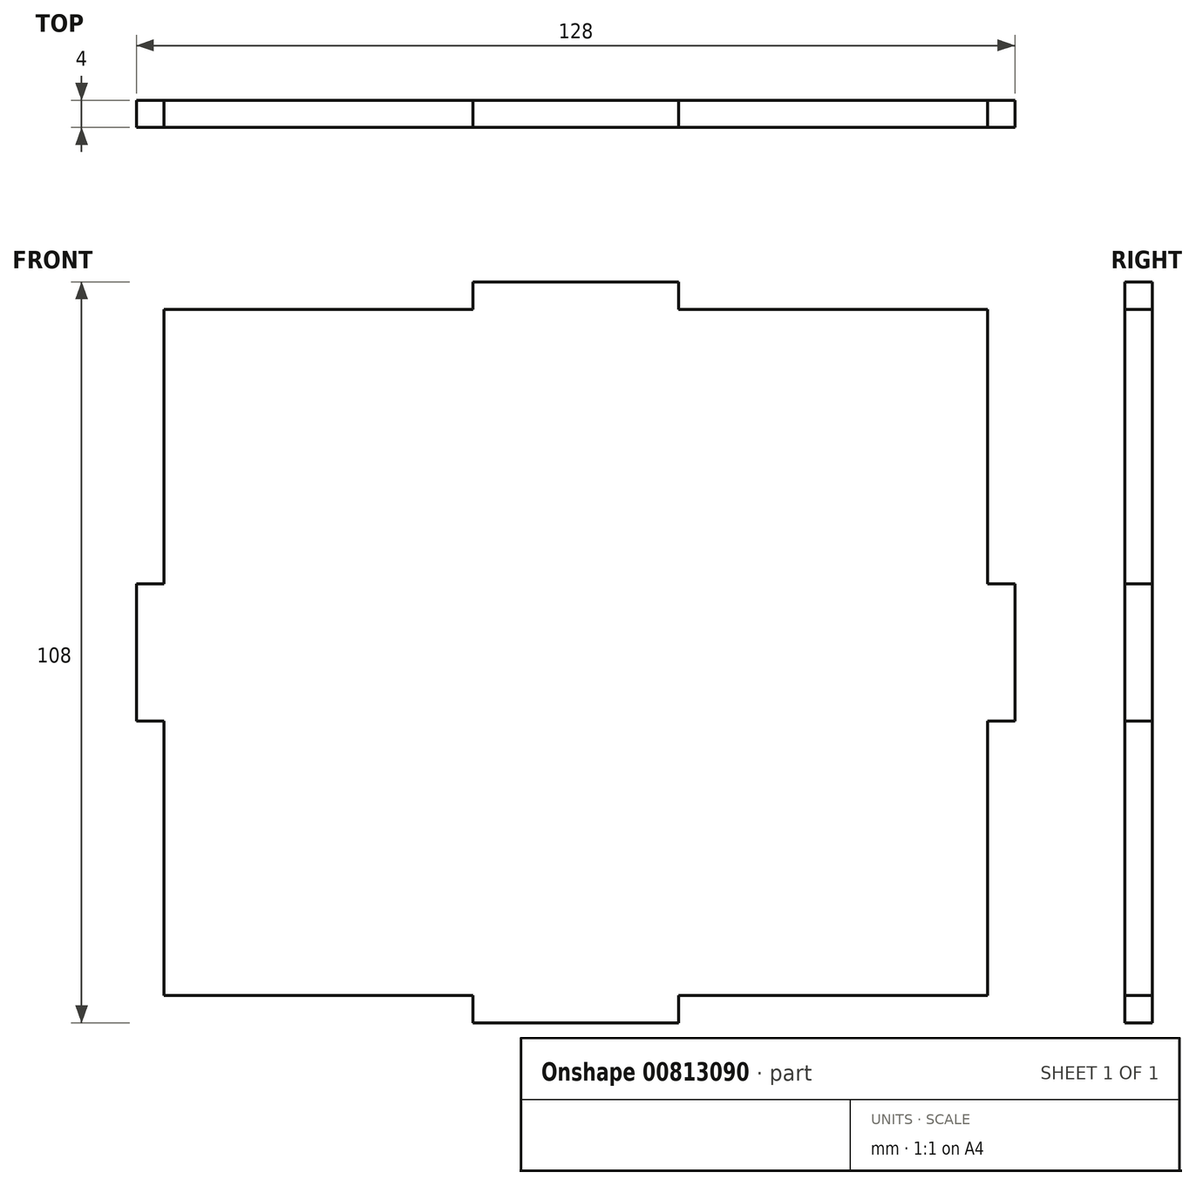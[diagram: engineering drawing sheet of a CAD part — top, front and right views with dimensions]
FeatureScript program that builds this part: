
annotation { "Feature Type Name" : "Feature", "Feature Type Description" : "" }
export const myFeature = defineFeature(function(context is Context, id is Id, definition is map)
    precondition{}
    {
        {
            var Q0;
            Q0=qCreatedBy(makeId("Front.planeOp"),FACE);
            var sketch = newSketch(context, id + "F0", { "sketchPlane" : qUnion([Q0])});
            skLineSegment(sketch, "E0.bottom", {"start": v(-60, 50) * mm, "end": v(-15, 50) * mm});
            skLineSegment(sketch, "E0.top", {"start": v(-60, -50) * mm, "end": v(-15, -50) * mm});
            skLineSegment(sketch, "E0.left", {"start": v(-60, 50) * mm, "end": v(-60, 10) * mm});
            skLineSegment(sketch, "E0.right", {"start": v(60, 50) * mm, "end": v(60, 10) * mm});
            skPoint(sketch, "E0.middle", {"position": v(0, 0) * mm});
            skLineSegment(sketch, "E1.bottom", {"start": v(-64, 10) * mm, "end": v(-60, 10) * mm});
            skLineSegment(sketch, "E1.top", {"start": v(-64, -10) * mm, "end": v(-60, -10) * mm});
            skLineSegment(sketch, "E1.left", {"start": v(-64, 10) * mm, "end": v(-64, -10) * mm});
            skLineSegment(sketch, "E1.right", {"start": v(64, 10) * mm, "end": v(64, -10) * mm});
            skLineSegment(sketch, "E2.bottom", {"start": v(-15, 54) * mm, "end": v(15, 54) * mm});
            skLineSegment(sketch, "E2.top", {"start": v(-15, -54) * mm, "end": v(15, -54) * mm});
            skLineSegment(sketch, "E2.left", {"start": v(-15, 54) * mm, "end": v(-15, 50) * mm});
            skLineSegment(sketch, "E2.right", {"start": v(15, 54) * mm, "end": v(15, 50) * mm});
            skLineSegment(sketch, "E3.trimOffspring", {"start": v(-15, -50) * mm, "end": v(-15, -54) * mm});
            skLineSegment(sketch, "E4.trimOffspring", {"start": v(15, 50) * mm, "end": v(60, 50) * mm});
            skLineSegment(sketch, "E5.trimOffspring", {"start": v(15, -50) * mm, "end": v(15, -54) * mm});
            skLineSegment(sketch, "E6.trimOffspring", {"start": v(60, 10) * mm, "end": v(64, 10) * mm});
            skLineSegment(sketch, "E7.trimOffspring", {"start": v(60, -10) * mm, "end": v(64, -10) * mm});
            skLineSegment(sketch, "E8.trimOffspring", {"start": v(60, -10) * mm, "end": v(60, -50) * mm});
            skLineSegment(sketch, "E9.trimOffspring", {"start": v(-60, -10) * mm, "end": v(-60, -50) * mm});
            skLineSegment(sketch, "E10.trimOffspring", {"start": v(15, -50) * mm, "end": v(60, -50) * mm});
            skSolve(sketch);
        }
        {
            var Q0;
            Q0=makeQuery(id+"F0.imprint","IMPRINT",FACE,{"disambiguationData":[TD([[makeQuery(id+"F0.imprint","IMPRINT",EDGE,{"derivedFrom":sQuery(id+"F0.wireOp",EDGE,"E0.bottom")}),-1.0]])]});
            extrude(context, id + "F1", {"entities" : qUnion([Q0]), "depth" : 4 * mm, "offsetDistance" : 25 * mm});
        }
    });
